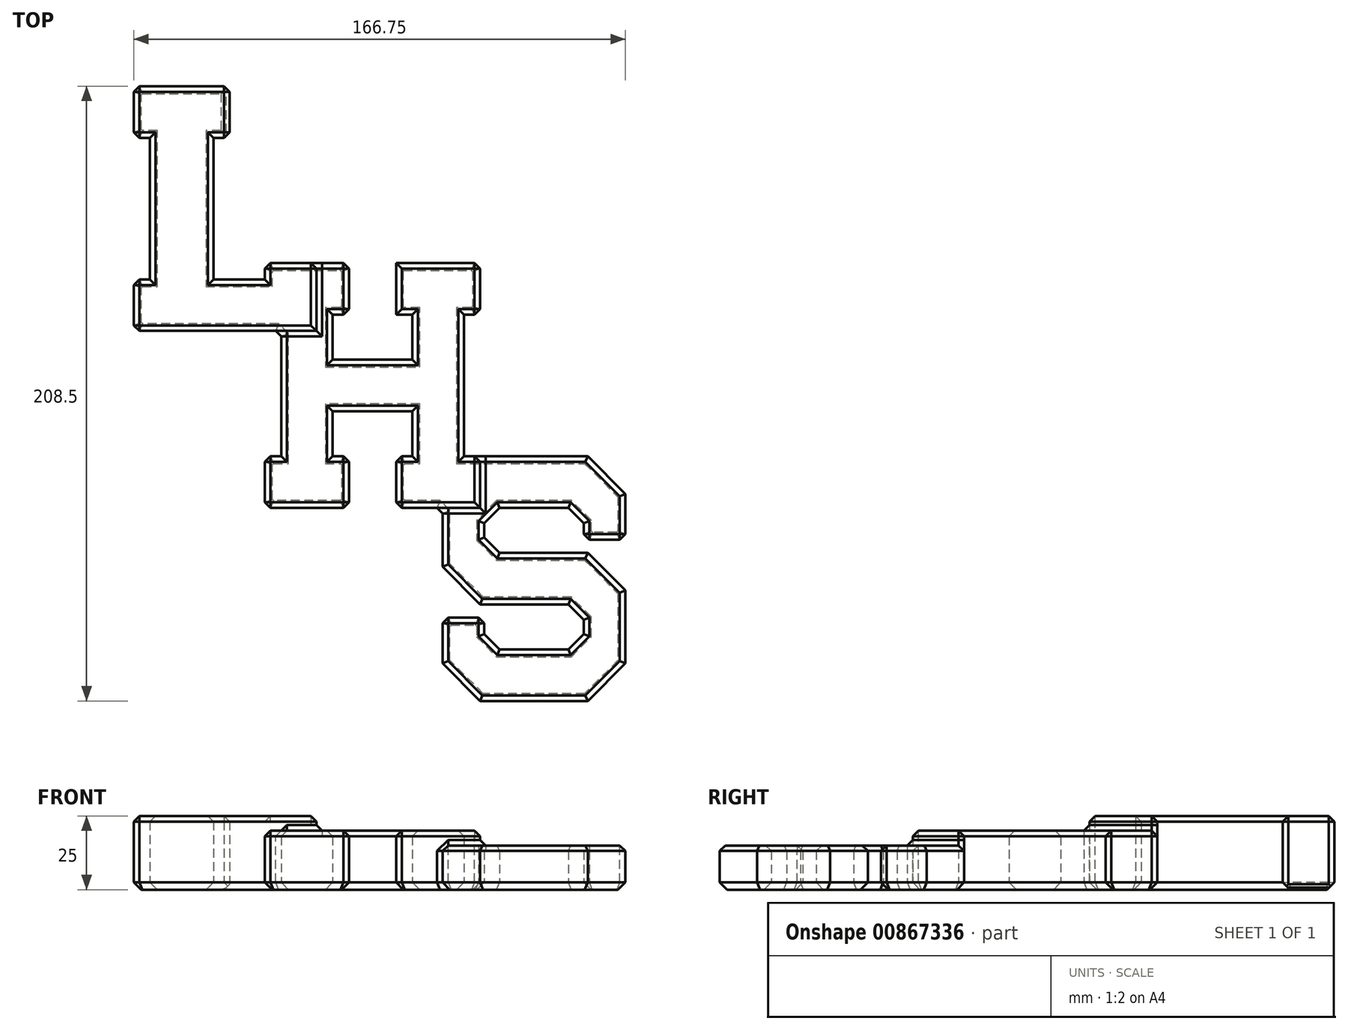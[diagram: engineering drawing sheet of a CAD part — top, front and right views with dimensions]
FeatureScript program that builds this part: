
annotation { "Feature Type Name" : "Feature", "Feature Type Description" : "" }
export const myFeature = defineFeature(function(context is Context, id is Id, definition is map)
    precondition{}
    {
        {
            var Q0;
            Q0=qCreatedBy(makeId("Top.planeOp"),FACE);
            var sketch = newSketch(context, id + "F0", { "sketchPlane" : qUnion([Q0])});
            skLineSegment(sketch, "E0", {"start": v(-84.76, 22.29) * mm, "end": v(-52.26, 22.29) * mm});
            skLineSegment(sketch, "E1", {"start": v(-52.26, 22.29) * mm, "end": v(-52.26, 4.79) * mm});
            skLineSegment(sketch, "E2", {"start": v(-52.26, 4.79) * mm, "end": v(-57.76, 4.79) * mm});
            skLineSegment(sketch, "E3", {"start": v(-57.76, 4.79) * mm, "end": v(-57.76, -43.21) * mm});
            skLineSegment(sketch, "E4", {"start": v(-57.76, -43.21) * mm, "end": v(-40.26, -43.21) * mm});
            skLineSegment(sketch, "E5", {"start": v(-40.26, -43.21) * mm, "end": v(-40.26, -37.71) * mm});
            skLineSegment(sketch, "E6", {"start": v(-40.26, -37.71) * mm, "end": v(-22.76, -37.71) * mm});
            skLineSegment(sketch, "E7", {"start": v(-22.76, -37.71) * mm, "end": v(-22.76, -60.71) * mm});
            skLineSegment(sketch, "E8", {"start": v(-22.76, -60.71) * mm, "end": v(-84.76, -60.71) * mm});
            skLineSegment(sketch, "E9", {"start": v(-84.76, -60.71) * mm, "end": v(-84.76, -43.21) * mm});
            skLineSegment(sketch, "E10", {"start": v(-84.76, -43.21) * mm, "end": v(-79.26, -43.21) * mm});
            skLineSegment(sketch, "E11", {"start": v(-79.26, -43.21) * mm, "end": v(-79.26, 4.79) * mm});
            skLineSegment(sketch, "E12", {"start": v(-79.26, 4.79) * mm, "end": v(-84.76, 4.79) * mm});
            skLineSegment(sketch, "E13", {"start": v(-84.76, 4.79) * mm, "end": v(-84.76, 22.29) * mm});
            skSolve(sketch);
        }
        {
            var Q0;
            Q0=qCreatedBy(makeId("Top.planeOp"),FACE);
            var sketch = newSketch(context, id + "F1", { "sketchPlane" : qUnion([Q0])});
            skLineSegment(sketch, "E14", {"start": v(-40.26, -37.71) * mm, "end": v(-11.76, -37.71) * mm});
            skLineSegment(sketch, "E15", {"start": v(-11.76, -37.71) * mm, "end": v(-11.76, -55.21) * mm});
            skLineSegment(sketch, "E16", {"start": v(-11.76, -55.21) * mm, "end": v(-17.26, -55.21) * mm});
            skLineSegment(sketch, "E17", {"start": v(-17.26, -55.21) * mm, "end": v(-17.26, -70.46) * mm});
            skLineSegment(sketch, "E18", {"start": v(-17.26, -70.46) * mm, "end": v(9.74, -70.46) * mm});
            skLineSegment(sketch, "E19", {"start": v(9.74, -70.46) * mm, "end": v(9.74, -55.21) * mm});
            skLineSegment(sketch, "E20", {"start": v(9.74, -55.21) * mm, "end": v(4.24, -55.21) * mm});
            skLineSegment(sketch, "E21", {"start": v(4.24, -55.21) * mm, "end": v(4.24, -37.71) * mm});
            skLineSegment(sketch, "E22", {"start": v(4.24, -37.71) * mm, "end": v(32.74, -37.71) * mm});
            skLineSegment(sketch, "E23", {"start": v(32.74, -37.71) * mm, "end": v(32.74, -55.21) * mm});
            skLineSegment(sketch, "E24", {"start": v(32.74, -55.21) * mm, "end": v(27.24, -55.21) * mm});
            skLineSegment(sketch, "E25", {"start": v(27.24, -55.21) * mm, "end": v(27.24, -103.21) * mm});
            skLineSegment(sketch, "E26", {"start": v(27.24, -103.21) * mm, "end": v(32.74, -103.21) * mm});
            skLineSegment(sketch, "E27", {"start": v(32.74, -103.21) * mm, "end": v(32.74, -120.71) * mm});
            skLineSegment(sketch, "E28", {"start": v(32.74, -120.71) * mm, "end": v(4.24, -120.71) * mm});
            skLineSegment(sketch, "E29", {"start": v(4.24, -120.71) * mm, "end": v(4.24, -103.21) * mm});
            skLineSegment(sketch, "E30", {"start": v(4.24, -103.21) * mm, "end": v(9.74, -103.21) * mm});
            skLineSegment(sketch, "E31", {"start": v(9.74, -103.21) * mm, "end": v(9.74, -87.96) * mm});
            skLineSegment(sketch, "E32", {"start": v(9.74, -87.96) * mm, "end": v(-17.26, -87.96) * mm});
            skLineSegment(sketch, "E33", {"start": v(-17.26, -87.96) * mm, "end": v(-17.26, -103.21) * mm});
            skLineSegment(sketch, "E34", {"start": v(-17.26, -103.21) * mm, "end": v(-11.76, -103.21) * mm});
            skLineSegment(sketch, "E35", {"start": v(-11.76, -103.21) * mm, "end": v(-11.76, -120.71) * mm});
            skLineSegment(sketch, "E36", {"start": v(-11.76, -120.71) * mm, "end": v(-40.26, -120.71) * mm});
            skLineSegment(sketch, "E37", {"start": v(-40.26, -120.71) * mm, "end": v(-40.26, -103.21) * mm});
            skLineSegment(sketch, "E38", {"start": v(-40.26, -103.21) * mm, "end": v(-34.76, -103.21) * mm});
            skLineSegment(sketch, "E39", {"start": v(-34.76, -103.21) * mm, "end": v(-34.76, -55.21) * mm});
            skLineSegment(sketch, "E40", {"start": v(-34.76, -55.21) * mm, "end": v(-40.26, -55.21) * mm});
            skLineSegment(sketch, "E41", {"start": v(-40.26, -55.21) * mm, "end": v(-40.26, -37.71) * mm});
            skLineSegment(sketch, "E42", {"start": v(-17.26, -70.46) * mm, "end": v(-17.26, -87.96) * mm, "construction": true});
            skLineSegment(sketch, "E43", {"start": v(-34.76, -55.21) * mm, "end": v(-17.26, -55.21) * mm, "construction": true});
            skLineSegment(sketch, "E44", {"start": v(9.74, -55.21) * mm, "end": v(27.24, -55.21) * mm, "construction": true});
            skPoint(sketch, "E45.0", {"position": v(-22.76, -37.71) * mm});
            skPoint(sketch, "E45.1", {"position": v(-40.26, -37.71) * mm});
            skLineSegment(sketch, "E46", {"start": v(-40.26, -37.71) * mm, "end": v(-22.76, -37.71) * mm, "construction": true});
            skSolve(sketch);
        }
        {
            var Q0;
            Q0=qCreatedBy(makeId("Top.planeOp"),FACE);
            var sketch = newSketch(context, id + "F2", { "sketchPlane" : qUnion([Q0])});
            skLineSegment(sketch, "E47", {"start": v(32.74, -103.21) * mm, "end": v(69.24, -103.21) * mm});
            skLineSegment(sketch, "E48", {"start": v(69.24, -103.21) * mm, "end": v(82, -115.96) * mm});
            skLineSegment(sketch, "E49", {"start": v(82, -115.96) * mm, "end": v(82, -131.46) * mm});
            skLineSegment(sketch, "E50", {"start": v(82, -131.46) * mm, "end": v(67.89, -131.46) * mm});
            skLineSegment(sketch, "E51", {"start": v(67.89, -131.46) * mm, "end": v(67.89, -125.96) * mm});
            skLineSegment(sketch, "E52", {"start": v(67.89, -125.96) * mm, "end": v(62.64, -120.71) * mm});
            skLineSegment(sketch, "E53", {"start": v(62.64, -120.71) * mm, "end": v(39.35, -120.71) * mm});
            skLineSegment(sketch, "E54", {"start": v(39.35, -120.71) * mm, "end": v(34.1, -125.96) * mm});
            skLineSegment(sketch, "E55", {"start": v(34.1, -125.96) * mm, "end": v(34.1, -130.71) * mm});
            skLineSegment(sketch, "E56", {"start": v(34.1, -130.71) * mm, "end": v(39.35, -135.96) * mm});
            skLineSegment(sketch, "E57", {"start": v(39.35, -135.96) * mm, "end": v(69.24, -135.96) * mm});
            skLineSegment(sketch, "E58", {"start": v(69.24, -135.96) * mm, "end": v(82, -148.71) * mm});
            skLineSegment(sketch, "E59", {"start": v(82, -148.71) * mm, "end": v(82, -173.46) * mm});
            skLineSegment(sketch, "E60", {"start": v(82, -173.46) * mm, "end": v(69.24, -186.21) * mm});
            skLineSegment(sketch, "E61", {"start": v(69.24, -186.21) * mm, "end": v(32.74, -186.21) * mm});
            skLineSegment(sketch, "E62", {"start": v(32.74, -186.21) * mm, "end": v(20, -173.46) * mm});
            skLineSegment(sketch, "E63", {"start": v(20, -173.46) * mm, "end": v(20, -157.96) * mm});
            skLineSegment(sketch, "E64", {"start": v(20, -157.96) * mm, "end": v(34.1, -157.96) * mm});
            skLineSegment(sketch, "E65", {"start": v(34.1, -157.96) * mm, "end": v(34.1, -163.46) * mm});
            skLineSegment(sketch, "E66", {"start": v(34.1, -163.46) * mm, "end": v(39.35, -168.71) * mm});
            skLineSegment(sketch, "E67", {"start": v(39.35, -168.71) * mm, "end": v(62.64, -168.71) * mm});
            skLineSegment(sketch, "E68", {"start": v(62.64, -168.71) * mm, "end": v(67.89, -163.46) * mm});
            skLineSegment(sketch, "E69", {"start": v(67.89, -163.46) * mm, "end": v(67.89, -158.71) * mm});
            skLineSegment(sketch, "E70", {"start": v(67.89, -158.71) * mm, "end": v(62.64, -153.46) * mm});
            skLineSegment(sketch, "E71", {"start": v(62.64, -153.46) * mm, "end": v(32.74, -153.46) * mm});
            skLineSegment(sketch, "E72", {"start": v(32.74, -153.46) * mm, "end": v(20, -140.71) * mm});
            skLineSegment(sketch, "E73", {"start": v(20, -140.71) * mm, "end": v(20, -115.96) * mm});
            skLineSegment(sketch, "E74", {"start": v(20, -115.96) * mm, "end": v(32.74, -103.21) * mm});
            skLineSegment(sketch, "E75", {"start": v(34.1, -125.96) * mm, "end": v(20, -125.96) * mm, "construction": true});
            skLineSegment(sketch, "E76", {"start": v(67.89, -125.96) * mm, "end": v(82, -125.96) * mm, "construction": true});
            skLineSegment(sketch, "E77", {"start": v(67.89, -163.46) * mm, "end": v(82, -163.46) * mm, "construction": true});
            skLineSegment(sketch, "E78", {"start": v(39.35, -168.71) * mm, "end": v(39.35, -186.21) * mm, "construction": true});
            skLineSegment(sketch, "E79", {"start": v(39.35, -120.71) * mm, "end": v(39.35, -103.21) * mm, "construction": true});
            skLineSegment(sketch, "E80", {"start": v(39.35, -135.96) * mm, "end": v(39.35, -153.46) * mm, "construction": true});
            skPoint(sketch, "E81.0", {"position": v(32.74, -103.21) * mm});
            skSolve(sketch);
        }
        {
            var Q0;
            Q0=makeQuery(id+"F0.imprint","IMPRINT",FACE,{"disambiguationData":[TD([[makeQuery(id+"F0.imprint","IMPRINT",EDGE,{"derivedFrom":sQuery(id+"F0.wireOp",EDGE,"E0")}),-1.0]])]});
            extrude(context, id + "F3", {"entities" : qUnion([Q0]), "depth" : 25 * mm, "offsetDistance" : 25 * mm});
        }
        {
            var Q0;
            Q0=makeQuery(id+"F1.imprint","IMPRINT",FACE,{"disambiguationData":[TD([[makeQuery(id+"F1.imprint","IMPRINT",EDGE,{"derivedFrom":sQuery(id+"F1.wireOp",EDGE,"E14")}),-1.0]])]});
            extrude(context, id + "F4", {"entities" : qUnion([Q0]), "operationType" : NewBodyOperationType.ADD, "depth" : 20 * mm, "offsetDistance" : 25 * mm});
        }
        {
            var Q0;
            Q0=makeQuery(id+"F2.imprint","IMPRINT",FACE,{"disambiguationData":[TD([[makeQuery(id+"F2.imprint","IMPRINT",EDGE,{"derivedFrom":sQuery(id+"F2.wireOp",EDGE,"E47")}),-1.0]])]});
            extrude(context, id + "F5", {"entities" : qUnion([Q0]), "operationType" : NewBodyOperationType.ADD, "depth" : 15 * mm, "offsetDistance" : 25 * mm});
        }
        {
            var Q0;
            Q0=makeQuery(id+"F3.opExtrude","CAP_FACE",FACE,{"disambiguationData":[OSD([sQuery(id+"F0.wireOp",EDGE,"E0"),sQuery(id+"F0.wireOp",EDGE,"E1"),sQuery(id+"F0.wireOp",EDGE,"E2"),sQuery(id+"F0.wireOp",EDGE,"E3"),sQuery(id+"F0.wireOp",EDGE,"E4"),sQuery(id+"F0.wireOp",EDGE,"E5"),sQuery(id+"F0.wireOp",EDGE,"E6"),sQuery(id+"F0.wireOp",EDGE,"E7"),sQuery(id+"F0.wireOp",EDGE,"E8"),sQuery(id+"F0.wireOp",EDGE,"E9"),sQuery(id+"F0.wireOp",EDGE,"E10"),sQuery(id+"F0.wireOp",EDGE,"E11"),sQuery(id+"F0.wireOp",EDGE,"E12"),sQuery(id+"F0.wireOp",EDGE,"E13")])],"isStart":false});
            var Q1;
            Q1=makeQuery(id+"F4.opExtrude","CAP_FACE",FACE,{"disambiguationData":[OSD([sQuery(id+"F1.wireOp",EDGE,"E14"),sQuery(id+"F1.wireOp",EDGE,"E15"),sQuery(id+"F1.wireOp",EDGE,"E16"),sQuery(id+"F1.wireOp",EDGE,"E17"),sQuery(id+"F1.wireOp",EDGE,"E18"),sQuery(id+"F1.wireOp",EDGE,"E19"),sQuery(id+"F1.wireOp",EDGE,"E20"),sQuery(id+"F1.wireOp",EDGE,"E21"),sQuery(id+"F1.wireOp",EDGE,"E22"),sQuery(id+"F1.wireOp",EDGE,"E23"),sQuery(id+"F1.wireOp",EDGE,"E24"),sQuery(id+"F1.wireOp",EDGE,"E25"),sQuery(id+"F1.wireOp",EDGE,"E26"),sQuery(id+"F1.wireOp",EDGE,"E27"),sQuery(id+"F1.wireOp",EDGE,"E28"),sQuery(id+"F1.wireOp",EDGE,"E29"),sQuery(id+"F1.wireOp",EDGE,"E30"),sQuery(id+"F1.wireOp",EDGE,"E31"),sQuery(id+"F1.wireOp",EDGE,"E32"),sQuery(id+"F1.wireOp",EDGE,"E33"),sQuery(id+"F1.wireOp",EDGE,"E34"),sQuery(id+"F1.wireOp",EDGE,"E35"),sQuery(id+"F1.wireOp",EDGE,"E36"),sQuery(id+"F1.wireOp",EDGE,"E37"),sQuery(id+"F1.wireOp",EDGE,"E38"),sQuery(id+"F1.wireOp",EDGE,"E39"),sQuery(id+"F1.wireOp",EDGE,"E40"),sQuery(id+"F1.wireOp",EDGE,"E41")])],"isStart":false});
            var Q2;
            Q2=makeQuery(id+"F5.opExtrude","CAP_FACE",FACE,{"disambiguationData":[OSD([sQuery(id+"F2.wireOp",EDGE,"E47"),sQuery(id+"F2.wireOp",EDGE,"E48"),sQuery(id+"F2.wireOp",EDGE,"E49"),sQuery(id+"F2.wireOp",EDGE,"E50"),sQuery(id+"F2.wireOp",EDGE,"E51"),sQuery(id+"F2.wireOp",EDGE,"E52"),sQuery(id+"F2.wireOp",EDGE,"E53"),sQuery(id+"F2.wireOp",EDGE,"E54"),sQuery(id+"F2.wireOp",EDGE,"E55"),sQuery(id+"F2.wireOp",EDGE,"E56"),sQuery(id+"F2.wireOp",EDGE,"E57"),sQuery(id+"F2.wireOp",EDGE,"E58"),sQuery(id+"F2.wireOp",EDGE,"E59"),sQuery(id+"F2.wireOp",EDGE,"E60"),sQuery(id+"F2.wireOp",EDGE,"E61"),sQuery(id+"F2.wireOp",EDGE,"E62"),sQuery(id+"F2.wireOp",EDGE,"E63"),sQuery(id+"F2.wireOp",EDGE,"E64"),sQuery(id+"F2.wireOp",EDGE,"E65"),sQuery(id+"F2.wireOp",EDGE,"E66"),sQuery(id+"F2.wireOp",EDGE,"E67"),sQuery(id+"F2.wireOp",EDGE,"E68"),sQuery(id+"F2.wireOp",EDGE,"E69"),sQuery(id+"F2.wireOp",EDGE,"E70"),sQuery(id+"F2.wireOp",EDGE,"E71"),sQuery(id+"F2.wireOp",EDGE,"E72"),sQuery(id+"F2.wireOp",EDGE,"E73"),sQuery(id+"F2.wireOp",EDGE,"E74")])],"isStart":false});
            var Q3;
            Q3=makeQuery(id+"F3.opExtrude","SWEPT_EDGE",EDGE,{"disambiguationData":[OSD([sQuery(id+"F0.wireOp",EDGE,"E12"),sQuery(id+"F0.wireOp",EDGE,"E13")])]});
            var Q4;
            Q4=makeQuery(id+"F3.opExtrude","SWEPT_EDGE",EDGE,{"disambiguationData":[OSD([sQuery(id+"F0.wireOp",EDGE,"E0"),sQuery(id+"F0.wireOp",EDGE,"E13")])]});
            var Q5;
            Q5=makeQuery(id+"F3.opExtrude","SWEPT_EDGE",EDGE,{"disambiguationData":[OSD([sQuery(id+"F0.wireOp",EDGE,"E9"),sQuery(id+"F0.wireOp",EDGE,"E10")])]});
            var Q6;
            Q6=makeQuery(id+"F3.opExtrude","SWEPT_EDGE",EDGE,{"disambiguationData":[OSD([sQuery(id+"F0.wireOp",EDGE,"E8"),sQuery(id+"F0.wireOp",EDGE,"E9")])]});
            var Q7;
            Q7=makeQuery(id+"F4.opExtrude","SWEPT_EDGE",EDGE,{"disambiguationData":[OSD([sQuery(id+"F1.wireOp",EDGE,"E37"),sQuery(id+"F1.wireOp",EDGE,"E38")])]});
            var Q8;
            Q8=makeQuery(id+"F4.opExtrude","SWEPT_EDGE",EDGE,{"disambiguationData":[OSD([sQuery(id+"F1.wireOp",EDGE,"E36"),sQuery(id+"F1.wireOp",EDGE,"E37")])]});
            var Q9;
            Q9=makeQuery(id+"F5.opExtrude","SWEPT_EDGE",EDGE,{"disambiguationData":[OSD([sQuery(id+"F2.wireOp",EDGE,"E63"),sQuery(id+"F2.wireOp",EDGE,"E64")])]});
            var Q10;
            Q10=makeQuery(id+"F3.opExtrude","SWEPT_FACE",FACE,{"disambiguationData":[OSD([sQuery(id+"F0.wireOp",EDGE,"E1")])]});
            var Q11;
            Q11=makeQuery(id+"F3.opExtrude","SWEPT_EDGE",EDGE,{"disambiguationData":[OSD([sQuery(id+"F0.wireOp",EDGE,"E1"),sQuery(id+"F0.wireOp",EDGE,"E2")])]});
            var Q12;
            Q12=makeQuery(id+"F4.opExtrude","SWEPT_EDGE",EDGE,{"disambiguationData":[OSD([sQuery(id+"F1.wireOp",EDGE,"E14"),sQuery(id+"F1.wireOp",EDGE,"E15")])]});
            var Q13;
            Q13=makeQuery(id+"F4.opExtrude","SWEPT_EDGE",EDGE,{"disambiguationData":[OSD([sQuery(id+"F1.wireOp",EDGE,"E15"),sQuery(id+"F1.wireOp",EDGE,"E16")])]});
            var Q14;
            Q14=makeQuery(id+"F3.opExtrude","SWEPT_EDGE",EDGE,{"disambiguationData":[OSD([sQuery(id+"F0.wireOp",EDGE,"E5"),sQuery(id+"F0.wireOp",EDGE,"E6")])]});
            var Q15;
            Q15=makeQuery(id+"F4.opExtrude","SWEPT_EDGE",EDGE,{"disambiguationData":[OSD([sQuery(id+"F1.wireOp",EDGE,"E22"),sQuery(id+"F1.wireOp",EDGE,"E23")])]});
            var Q16;
            Q16=makeQuery(id+"F4.opExtrude","SWEPT_EDGE",EDGE,{"disambiguationData":[OSD([sQuery(id+"F1.wireOp",EDGE,"E23"),sQuery(id+"F1.wireOp",EDGE,"E24")])]});
            var Q17;
            Q17=makeQuery(id+"F4.opExtrude","SWEPT_EDGE",EDGE,{"disambiguationData":[OSD([sQuery(id+"F1.wireOp",EDGE,"E34"),sQuery(id+"F1.wireOp",EDGE,"E35")])]});
            var Q18;
            Q18=makeQuery(id+"F4.opExtrude","SWEPT_EDGE",EDGE,{"disambiguationData":[OSD([sQuery(id+"F1.wireOp",EDGE,"E35"),sQuery(id+"F1.wireOp",EDGE,"E36")])]});
            var Q19;
            Q19=makeQuery(id+"F4.opExtrude","SWEPT_EDGE",EDGE,{"disambiguationData":[OSD([sQuery(id+"F1.wireOp",EDGE,"E29"),sQuery(id+"F1.wireOp",EDGE,"E30")])]});
            var Q20;
            Q20=makeQuery(id+"F5.opExtrude","SWEPT_EDGE",EDGE,{"disambiguationData":[OSD([sQuery(id+"F2.wireOp",EDGE,"E49"),sQuery(id+"F2.wireOp",EDGE,"E50")])]});
            var Q21;
            Q21=makeQuery(id+"F5.opExtrude","SWEPT_EDGE",EDGE,{"disambiguationData":[OSD([sQuery(id+"F2.wireOp",EDGE,"E64"),sQuery(id+"F2.wireOp",EDGE,"E65")])]});
            var Q22;
            Q22=makeQuery(id+"F4.opExtrude","SWEPT_EDGE",EDGE,{"disambiguationData":[OSD([sQuery(id+"F1.wireOp",EDGE,"E28"),sQuery(id+"F1.wireOp",EDGE,"E29")])]});
            var Q23;
            Q23=makeQuery(id+"F5.opExtrude","SWEPT_EDGE",EDGE,{"disambiguationData":[OSD([sQuery(id+"F2.wireOp",EDGE,"E50"),sQuery(id+"F2.wireOp",EDGE,"E51")])]});
            chamfer(context, id + "F6", {"entities" : qUnion([Q0, Q1, Q2, Q3, Q4, Q5, Q6, Q7, Q8, Q9, Q10, Q11, Q12, Q13, Q14, Q15, Q16, Q17, Q18, Q19, Q20, Q21, Q22, Q23]), "width" : 1.9 * mm, "tangentPropagation" : true});
        }
        {
            var Q0;
            Q0=makeQuery(id+"F5.boolean.opBoolean","MERGE",FACE,{"derivedFrom":[makeQuery(id+"F4.boolean.opBoolean","MERGE",FACE,{"derivedFrom":[makeQuery(id+"F3.opExtrude","CAP_FACE",FACE,{"disambiguationData":[OSD([sQuery(id+"F0.wireOp",EDGE,"E0"),sQuery(id+"F0.wireOp",EDGE,"E1"),sQuery(id+"F0.wireOp",EDGE,"E2"),sQuery(id+"F0.wireOp",EDGE,"E3"),sQuery(id+"F0.wireOp",EDGE,"E4"),sQuery(id+"F0.wireOp",EDGE,"E5"),sQuery(id+"F0.wireOp",EDGE,"E6"),sQuery(id+"F0.wireOp",EDGE,"E7"),sQuery(id+"F0.wireOp",EDGE,"E8"),sQuery(id+"F0.wireOp",EDGE,"E9"),sQuery(id+"F0.wireOp",EDGE,"E10"),sQuery(id+"F0.wireOp",EDGE,"E11"),sQuery(id+"F0.wireOp",EDGE,"E12"),sQuery(id+"F0.wireOp",EDGE,"E13")])],"isStart":true}),makeQuery(id+"F4.opExtrude","CAP_FACE",FACE,{"disambiguationData":[OSD([sQuery(id+"F1.wireOp",EDGE,"E14"),sQuery(id+"F1.wireOp",EDGE,"E15"),sQuery(id+"F1.wireOp",EDGE,"E16"),sQuery(id+"F1.wireOp",EDGE,"E17"),sQuery(id+"F1.wireOp",EDGE,"E18"),sQuery(id+"F1.wireOp",EDGE,"E19"),sQuery(id+"F1.wireOp",EDGE,"E20"),sQuery(id+"F1.wireOp",EDGE,"E21"),sQuery(id+"F1.wireOp",EDGE,"E22"),sQuery(id+"F1.wireOp",EDGE,"E23"),sQuery(id+"F1.wireOp",EDGE,"E24"),sQuery(id+"F1.wireOp",EDGE,"E25"),sQuery(id+"F1.wireOp",EDGE,"E26"),sQuery(id+"F1.wireOp",EDGE,"E27"),sQuery(id+"F1.wireOp",EDGE,"E28"),sQuery(id+"F1.wireOp",EDGE,"E29"),sQuery(id+"F1.wireOp",EDGE,"E30"),sQuery(id+"F1.wireOp",EDGE,"E31"),sQuery(id+"F1.wireOp",EDGE,"E32"),sQuery(id+"F1.wireOp",EDGE,"E33"),sQuery(id+"F1.wireOp",EDGE,"E34"),sQuery(id+"F1.wireOp",EDGE,"E35"),sQuery(id+"F1.wireOp",EDGE,"E36"),sQuery(id+"F1.wireOp",EDGE,"E37"),sQuery(id+"F1.wireOp",EDGE,"E38"),sQuery(id+"F1.wireOp",EDGE,"E39"),sQuery(id+"F1.wireOp",EDGE,"E40"),sQuery(id+"F1.wireOp",EDGE,"E41")])],"isStart":true})]}),makeQuery(id+"F5.opExtrude","CAP_FACE",FACE,{"disambiguationData":[OSD([sQuery(id+"F2.wireOp",EDGE,"E47"),sQuery(id+"F2.wireOp",EDGE,"E48"),sQuery(id+"F2.wireOp",EDGE,"E49"),sQuery(id+"F2.wireOp",EDGE,"E50"),sQuery(id+"F2.wireOp",EDGE,"E51"),sQuery(id+"F2.wireOp",EDGE,"E52"),sQuery(id+"F2.wireOp",EDGE,"E53"),sQuery(id+"F2.wireOp",EDGE,"E54"),sQuery(id+"F2.wireOp",EDGE,"E55"),sQuery(id+"F2.wireOp",EDGE,"E56"),sQuery(id+"F2.wireOp",EDGE,"E57"),sQuery(id+"F2.wireOp",EDGE,"E58"),sQuery(id+"F2.wireOp",EDGE,"E59"),sQuery(id+"F2.wireOp",EDGE,"E60"),sQuery(id+"F2.wireOp",EDGE,"E61"),sQuery(id+"F2.wireOp",EDGE,"E62"),sQuery(id+"F2.wireOp",EDGE,"E63"),sQuery(id+"F2.wireOp",EDGE,"E64"),sQuery(id+"F2.wireOp",EDGE,"E65"),sQuery(id+"F2.wireOp",EDGE,"E66"),sQuery(id+"F2.wireOp",EDGE,"E67"),sQuery(id+"F2.wireOp",EDGE,"E68"),sQuery(id+"F2.wireOp",EDGE,"E69"),sQuery(id+"F2.wireOp",EDGE,"E70"),sQuery(id+"F2.wireOp",EDGE,"E71"),sQuery(id+"F2.wireOp",EDGE,"E72"),sQuery(id+"F2.wireOp",EDGE,"E73"),sQuery(id+"F2.wireOp",EDGE,"E74")])],"isStart":true})]});
            chamfer(context, id + "F7", {"entities" : qUnion([Q0]), "width" : 2.5 * mm, "tangentPropagation" : true});
        }
    });
